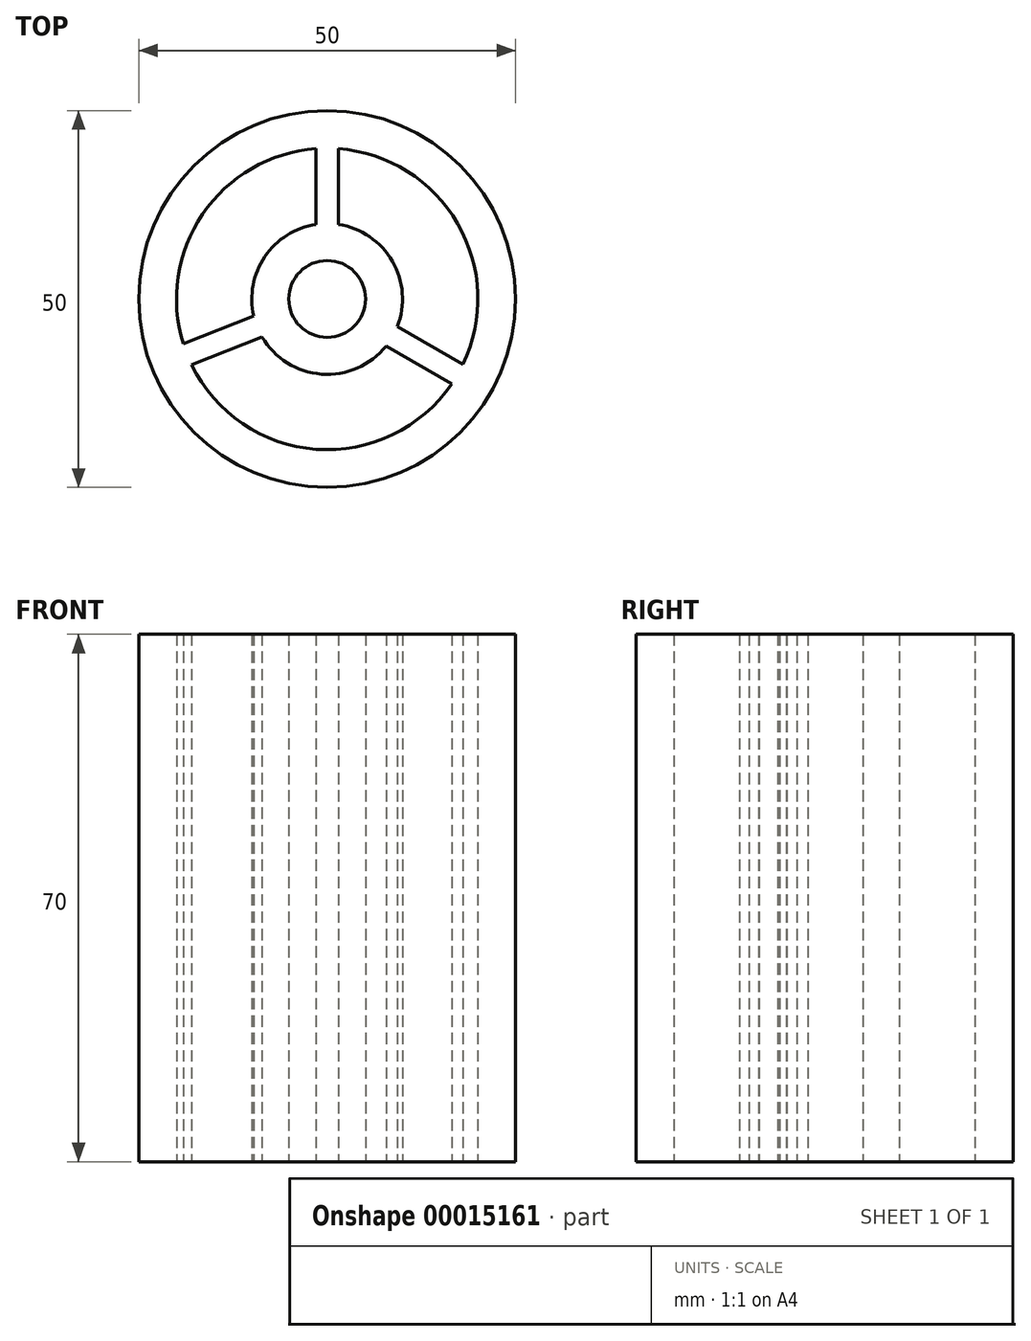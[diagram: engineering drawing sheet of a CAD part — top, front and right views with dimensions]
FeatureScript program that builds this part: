
annotation { "Feature Type Name" : "Feature", "Feature Type Description" : "" }
export const myFeature = defineFeature(function(context is Context, id is Id, definition is map)
    precondition{}
    {
        {
            var Q0;
            Q0=qCreatedBy(makeId("Top.planeOp"),FACE);
            var sketch = newSketch(context, id + "F0", { "sketchPlane" : qUnion([Q0])});
            skCircle(sketch, "E0", {"center": v(0, 0) * mm, "radius": 25 * mm});
            skCircle(sketch, "E1", {"center": v(0, 0) * mm, "radius": 5.1 * mm});
            skLineSegment(sketch, "E2", {"start": v(1.5, 14.92) * mm, "end": v(1.5, 9.89) * mm});
            skLineSegment(sketch, "E3", {"start": v(-1.5, 14.92) * mm, "end": v(-1.5, 9.89) * mm});
            skLineSegment(sketch, "E4", {"start": v(9.31, -3.64) * mm, "end": v(13.68, -6.16) * mm});
            skLineSegment(sketch, "E5", {"start": v(-13.32, -6.89) * mm, "end": v(-8.64, -5.03) * mm});
            skLineSegment(sketch, "E6", {"start": v(-14.43, -4.1) * mm, "end": v(-9.74, -2.25) * mm});
            skLineSegment(sketch, "E7", {"start": v(7.81, -6.24) * mm, "end": v(12.18, -8.76) * mm});
            skArc(sketch, "E8", {"start": v(18.02, -8.67) * mm, "mid": v(17.32, 10) * mm, "end": v(1.5, 19.94) * mm});
            skLineSegment(sketch, "E9", {"start": v(1.5, 14.92) * mm, "end": v(1.5, 19.94) * mm});
            skLineSegment(sketch, "E10", {"start": v(-1.5, 14.92) * mm, "end": v(-1.5, 19.94) * mm});
            skLineSegment(sketch, "E11", {"start": v(13.68, -6.16) * mm, "end": v(18.02, -8.67) * mm});
            skLineSegment(sketch, "E12", {"start": v(12.18, -8.76) * mm, "end": v(16.52, -11.27) * mm});
            skLineSegment(sketch, "E13", {"start": v(-14.43, -4.1) * mm, "end": v(-19.1, -5.95) * mm});
            skLineSegment(sketch, "E14", {"start": v(-13.32, -6.89) * mm, "end": v(-18, -8.74) * mm});
            skArc(sketch, "E15.trimOffspring", {"start": v(-1.5, 19.94) * mm, "mid": v(-16.54, 11.24) * mm, "end": v(-19.1, -5.95) * mm});
            skArc(sketch, "E16.trimOffspring", {"start": v(-18, -8.74) * mm, "mid": v(-1.46, -19.95) * mm, "end": v(16.52, -11.27) * mm});
            skArc(sketch, "E17", {"start": v(9.31, -3.64) * mm, "mid": v(8.66, 5) * mm, "end": v(1.5, 9.89) * mm});
            skPoint(sketch, "E18.orphan", {"position": v(-6.28, -4.1) * mm});
            skPoint(sketch, "E19.orphan", {"position": v(-1.5, 7.35) * mm});
            skPoint(sketch, "E20.orphan", {"position": v(1.5, 7.35) * mm});
            skArc(sketch, "E21.trimOffspring", {"start": v(-1.5, 9.89) * mm, "mid": v(-8.27, 5.62) * mm, "end": v(-9.74, -2.25) * mm});
            skArc(sketch, "E22.trimOffspring", {"start": v(-8.64, -5.03) * mm, "mid": v(-0.73, -9.97) * mm, "end": v(7.81, -6.24) * mm});
            skSolve(sketch);
        }
        {
            var Q0;
            Q0=makeQuery(id+"F0.imprint","IMPRINT",FACE,{"disambiguationData":[TD([[makeQuery(id+"F0.imprint","IMPRINT",EDGE,{"derivedFrom":sQuery(id+"F0.wireOp",EDGE,"E0")}),1.0]])]});
            extrude(context, id + "F1", {"entities" : qUnion([Q0]), "depth" : 70 * mm});
        }
    });
